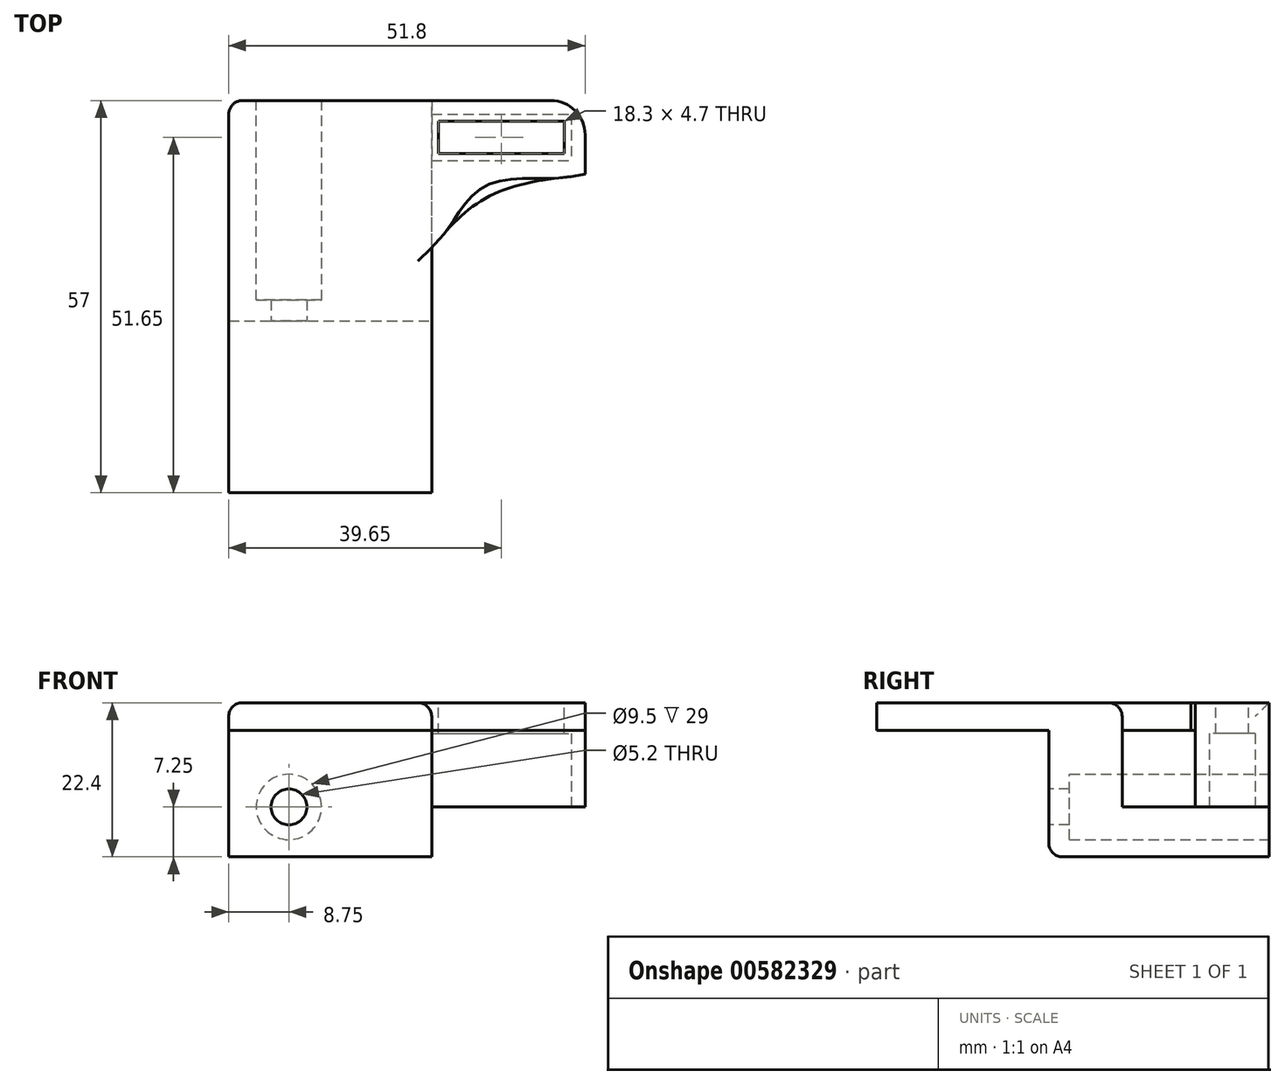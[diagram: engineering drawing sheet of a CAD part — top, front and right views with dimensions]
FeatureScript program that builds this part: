
annotation { "Feature Type Name" : "Feature", "Feature Type Description" : "" }
export const myFeature = defineFeature(function(context is Context, id is Id, definition is map)
    precondition{}
    {
        {
            var Q0;
            Q0=qCreatedBy(makeId("Front.planeOp"),FACE);
            var sketch = newSketch(context, id + "F0", { "sketchPlane" : qUnion([Q0])});
            skLineSegment(sketch, "E0.bottom", {"start": v(8.75, 10.25) * mm, "end": v(-8.75, 10.25) * mm});
            skLineSegment(sketch, "E0.top", {"start": v(8.75, -10.25) * mm, "end": v(3.25, -10.25) * mm});
            skLineSegment(sketch, "E0.left", {"start": v(8.75, 10.25) * mm, "end": v(8.75, -10.25) * mm});
            skLineSegment(sketch, "E0.right", {"start": v(-8.75, 10.25) * mm, "end": v(-8.75, 1.75) * mm});
            skPoint(sketch, "E0.middle", {"position": v(0, 0) * mm});
            skCircle(sketch, "E1", {"center": v(0, 0) * mm, "radius": 4.75 * mm});
            skLineSegment(sketch, "E2", {"start": v(8.75, 10.25) * mm, "end": v(20.75, 10.25) * mm});
            skLineSegment(sketch, "E3", {"start": v(20.75, 10.25) * mm, "end": v(20.75, -10.25) * mm});
            skLineSegment(sketch, "E4", {"start": v(8.75, -10.25) * mm, "end": v(20.75, -10.25) * mm});
            skPoint(sketch, "E5.visualSharp", {"position": v(-8.75, -10.25) * mm});
            skLineSegment(sketch, "E6", {"start": v(-8.75, 1.75) * mm, "end": v(-8.75, -10.25) * mm});
            skLineSegment(sketch, "E7", {"start": v(3.25, -10.25) * mm, "end": v(-8.75, -10.25) * mm});
            skSolve(sketch);
        }
        {
            var Q0;
            Q0 = qSketchRegion(id + "F0", true);
            extrude(context, id + "F1", {"entities" : qUnion([Q0]), "depth" : 30 * mm, "offsetDistance" : 25 * mm});
        }
        {
            var Q0;
            Q0=makeQuery(id+"F1.opExtrude","SWEPT_FACE",FACE,{"disambiguationData":[OSD([sQuery(id+"F0.wireOp",EDGE,"E0.top"),sQuery(id+"F0.wireOp",EDGE,"E4")])]});
            cPlane(context, id + "F2", {"entities" : qUnion([Q0]), "cplaneType" : CPlaneType.OFFSET, "offset" : 10.25 * mm, "oppositeDirection" : true, "width" : 150 * mm, "height" : 150 * mm});
        }
        {
            var Q0;
            Q0=qCreatedBy(id+"F2.planeOp",FACE);
            var sketch = newSketch(context, id + "F3", { "sketchPlane" : qUnion([Q0])});
            skLineSegment(sketch, "E8.bottom", {"start": v(20.75, 0) * mm, "end": v(41.05, 0) * mm});
            skLineSegment(sketch, "E8.top", {"start": v(20.75, 6.7) * mm, "end": v(41.05, 6.7) * mm});
            skLineSegment(sketch, "E8.left", {"start": v(20.75, 0) * mm, "end": v(20.75, 6.7) * mm});
            skLineSegment(sketch, "E8.right", {"start": v(41.05, 0) * mm, "end": v(41.05, 6.7) * mm});
            skLineSegment(sketch, "E9.0", {"start": v(18.75, -2) * mm, "end": v(43.05, -2) * mm});
            skLineSegment(sketch, "E9.1", {"start": v(18.75, -2) * mm, "end": v(18.75, 8.7) * mm});
            skLineSegment(sketch, "E9.2", {"start": v(18.75, 8.7) * mm, "end": v(43.05, 8.7) * mm});
            skLineSegment(sketch, "E9.3", {"start": v(43.05, -2) * mm, "end": v(43.05, 8.7) * mm});
            skSolve(sketch);
        }
        {
            var Q0;
            Q0 = qSketchRegion(id + "F3", true);
            extrude(context, id + "F4", {"entities" : qUnion([Q0]), "operationType" : NewBodyOperationType.ADD, "oppositeDirection" : true, "depth" : 11.15 * mm, "offsetDistance" : 25 * mm});
        }
        {
            var Q0;
            Q0=makeQuery(id+"F4.opExtrude","CAP_FACE",FACE,{"disambiguationData":[OSD([sQuery(id+"F3.wireOp",EDGE,"E8.bottom"),sQuery(id+"F3.wireOp",EDGE,"E8.top"),sQuery(id+"F3.wireOp",EDGE,"E8.left"),sQuery(id+"F3.wireOp",EDGE,"E8.right"),sQuery(id+"F3.wireOp",EDGE,"E9.0"),sQuery(id+"F3.wireOp",EDGE,"E9.1"),sQuery(id+"F3.wireOp",EDGE,"E9.2"),sQuery(id+"F3.wireOp",EDGE,"E9.3")])],"isStart":false});
            var sketch = newSketch(context, id + "F5", { "sketchPlane" : qUnion([Q0])});
            skLineSegment(sketch, "E10.0", {"start": v(40.05, -1) * mm, "end": v(40.05, -5.7) * mm});
            skLineSegment(sketch, "E10.1", {"start": v(21.75, -1) * mm, "end": v(40.05, -1) * mm});
            skLineSegment(sketch, "E10.2", {"start": v(21.75, -1) * mm, "end": v(21.75, -5.7) * mm});
            skLineSegment(sketch, "E11.0", {"start": v(21.75, -5.7) * mm, "end": v(40.05, -5.7) * mm});
            skSolve(sketch);
        }
        {
            var Q0;
            Q0=makeQuery(id+"F5.imprint","IMPRINT",FACE,{"disambiguationData":[TD([[makeQuery(id+"F5.imprint","IMPRINT",EDGE,{"derivedFrom":sQuery(id+"F5.wireOp",EDGE,"E10.0")}),1.0]])]});
            extrude(context, id + "F6", {"entities" : qUnion([Q0]), "operationType" : NewBodyOperationType.ADD, "oppositeDirection" : true, "depth" : 0.5 * mm, "offsetDistance" : 25 * mm});
        }
        {
            var Q0;
            Q0=makeQuery(id+"F1.opExtrude","CAP_FACE",FACE,{"disambiguationData":[OSD([sQuery(id+"F0.wireOp",EDGE,"E0.bottom"),sQuery(id+"F0.wireOp",EDGE,"E0.top"),sQuery(id+"F0.wireOp",EDGE,"E0.right"),sQuery(id+"F0.wireOp",EDGE,"E1"),sQuery(id+"F0.wireOp",EDGE,"E2"),sQuery(id+"F0.wireOp",EDGE,"E3"),sQuery(id+"F0.wireOp",EDGE,"E4"),sQuery(id+"F0.wireOp",EDGE,"E5.filletArc")])],"isStart":true});
            var sketch = newSketch(context, id + "F7", { "sketchPlane" : qUnion([Q0])});
            skLineSegment(sketch, "E12.0", {"start": v(8.75, 10.25) * mm, "end": v(-18.75, 10.25) * mm});
            skLineSegment(sketch, "E13.0", {"start": v(8.75, 10.25) * mm, "end": v(8.75, 10.25) * mm});
            skLineSegment(sketch, "E14.0", {"start": v(-3.25, -10.25) * mm, "end": v(-20.75, -10.25) * mm});
            skPoint(sketch, "E15.0", {"position": v(-20.75, -5.12) * mm});
            skLineSegment(sketch, "E16.0", {"start": v(-20.75, 0) * mm, "end": v(-20.75, -10.25) * mm});
            skLineSegment(sketch, "E17.0.0", {"start": v(-20.75, 0) * mm, "end": v(-18.75, 0) * mm});
            skLineSegment(sketch, "E17.0.1", {"start": v(-18.75, 0) * mm, "end": v(-18.75, 10.25) * mm});
            skCircle(sketch, "E18.0", {"center": v(0, 0) * mm, "radius": 4.75 * mm});
            skPoint(sketch, "E17.0.2.end.orphan", {"position": v(-43.05, 11.15) * mm});
            skPoint(sketch, "E17.0.2.start.orphan", {"position": v(-18.75, 11.15) * mm});
            skPoint(sketch, "E19.orphan", {"position": v(-43.05, 0) * mm});
            skLineSegment(sketch, "E20.0", {"start": v(8.75, 10.25) * mm, "end": v(8.75, -10.25) * mm});
            skLineSegment(sketch, "E21.0", {"start": v(8.75, -10.25) * mm, "end": v(-20.75, -10.25) * mm});
            skSolve(sketch);
        }
        {
            var Q0;
            Q0 = qSketchRegion(id + "F7", true);
            extrude(context, id + "F8", {"entities" : qUnion([Q0]), "operationType" : NewBodyOperationType.ADD, "depth" : 2 * mm, "offsetDistance" : 25 * mm});
        }
        {
            var Q0;
            Q0=makeQuery(id+"F8.boolean.opBoolean","MERGE",FACE,{"derivedFrom":[makeQuery(id+"F1.opExtrude","SWEPT_FACE",FACE,{"disambiguationData":[OSD([sQuery(id+"F0.wireOp",EDGE,"E0.bottom"),sQuery(id+"F0.wireOp",EDGE,"E2")])]}),makeQuery(id+"F8.opExtrude","SWEPT_FACE",FACE,{"disambiguationData":[OSD([sQuery(id+"F7.wireOp",EDGE,"E12.0")])]})]});
            var sketch = newSketch(context, id + "F9", { "sketchPlane" : qUnion([Q0])});
            skLineSegment(sketch, "E22.0", {"start": v(18.75, -8.7) * mm, "end": v(18.75, 2) * mm});
            skLineSegment(sketch, "E23.0", {"start": v(18.75, -8.7) * mm, "end": v(20.75, -8.7) * mm});
            skLineSegment(sketch, "E24.0", {"start": v(20.75, -30) * mm, "end": v(20.75, -8.7) * mm});
            skLineSegment(sketch, "E25.0", {"start": v(-8.75, 2) * mm, "end": v(18.75, 2) * mm});
            skLineSegment(sketch, "E26.0", {"start": v(-8.75, -30) * mm, "end": v(-8.75, 2) * mm});
            skLineSegment(sketch, "E27.0", {"start": v(-8.75, -30) * mm, "end": v(20.75, -30) * mm});
            skPoint(sketch, "E28.orphan", {"position": v(43.05, -8.7) * mm});
            skSolve(sketch);
        }
        {
            var Q0;
            Q0 = qSketchRegion(id + "F9", true);
            var Q1;
            {var subQ0=sQuery(id+"F3.wireOp",EDGE,"E8.right");var subQ1=sQuery(id+"F3.wireOp",EDGE,"E8.left");var subQ2=sQuery(id+"F3.wireOp",EDGE,"E8.top");var subQ3=sQuery(id+"F3.wireOp",EDGE,"E8.bottom");Q1=makeQuery(id+"F6.boolean.opBoolean","MERGE",FACE,{"derivedFrom":[makeQuery(id+"F4.opExtrude","CAP_FACE",FACE,{"disambiguationData":[OSD([subQ3,subQ2,subQ1,subQ0,sQuery(id+"F3.wireOp",EDGE,"E9.0"),sQuery(id+"F3.wireOp",EDGE,"E9.1"),sQuery(id+"F3.wireOp",EDGE,"E9.2"),sQuery(id+"F3.wireOp",EDGE,"E9.3")])],"isStart":false}),makeQuery(id+"F6.opExtrude","CAP_FACE",FACE,{"disambiguationData":[OSD([subQ3,subQ2,subQ1,subQ0,sQuery(id+"F5.wireOp",EDGE,"E10.0"),sQuery(id+"F5.wireOp",EDGE,"E10.1"),sQuery(id+"F5.wireOp",EDGE,"E10.2"),sQuery(id+"F5.wireOp",EDGE,"E11.0")])],"isStart":true})]});}
            extrude(context, id + "F10", {"entities" : qUnion([Q0]), "operationType" : NewBodyOperationType.ADD, "endBound" : BoundingType.UP_TO_SURFACE, "depth" : 1 * mm, "endBoundEntityFace" : qUnion([Q1]), "offsetDistance" : 25 * mm});
        }
        {
            var Q0;
            {var subQ0=sQuery(id+"F5.wireOp",EDGE,"E11.0");var subQ1=sQuery(id+"F5.wireOp",EDGE,"E10.2");var subQ2=sQuery(id+"F5.wireOp",EDGE,"E10.1");var subQ3=sQuery(id+"F5.wireOp",EDGE,"E10.0");var subQ4=sQuery(id+"F3.wireOp",EDGE,"E9.3");var subQ5=sQuery(id+"F3.wireOp",EDGE,"E9.2");var subQ6=sQuery(id+"F3.wireOp",EDGE,"E9.1");var subQ7=sQuery(id+"F3.wireOp",EDGE,"E9.0");var subQ8=sQuery(id+"F3.wireOp",EDGE,"E8.right");var subQ9=sQuery(id+"F3.wireOp",EDGE,"E8.left");var subQ10=sQuery(id+"F3.wireOp",EDGE,"E8.top");var subQ11=sQuery(id+"F3.wireOp",EDGE,"E8.bottom");Q0=makeQuery(id+"F10.boolean.opBoolean","MERGE",FACE,{"derivedFrom":[makeQuery(id+"F6.boolean.opBoolean","MERGE",FACE,{"derivedFrom":[makeQuery(id+"F4.opExtrude","CAP_FACE",FACE,{"disambiguationData":[OSD([subQ11,subQ10,subQ9,subQ8,subQ7,subQ6,subQ5,subQ4])],"isStart":false}),makeQuery(id+"F6.opExtrude","CAP_FACE",FACE,{"disambiguationData":[OSD([subQ11,subQ10,subQ9,subQ8,subQ3,subQ2,subQ1,subQ0])],"isStart":true})]}),makeQuery(id+"F10.opExtrude","CAP_FACE",FACE,{"disambiguationData":[OSD([subQ11,subQ10,subQ9,subQ8,subQ7,subQ6,subQ5,subQ4,subQ3,subQ2,subQ1,subQ0])],"isStart":false})]});}
            var sketch = newSketch(context, id + "F11", { "sketchPlane" : qUnion([Q0])});
            skPoint(sketch, "E29.endSnap0", {"position": v(20.75, -19.35) * mm});
            skFitSpline(sketch, "E30", {"points": [v(43.05, -8.7) * mm, v(29.05, -11.93) * mm, v(20.75, -19.35) * mm], "startDerivative": vector(-28.6, -3.49) * mm, "endDerivative": vector(-15.73, -18.12) * mm});
            skLineSegment(sketch, "E31", {"start": v(20.75, -19.35) * mm, "end": v(20.75, -8.7) * mm});
            skLineSegment(sketch, "E32", {"start": v(20.75, -8.7) * mm, "end": v(43.05, -8.7) * mm});
            skSolve(sketch);
        }
        {
            var Q0;
            Q0 = qSketchRegion(id + "F11", true);
            var Q1;
            Q1=qCreatedBy(makeId("Top.planeOp"),FACE);
            extrude(context, id + "F12", {"entities" : qUnion([Q0]), "operationType" : NewBodyOperationType.ADD, "endBound" : BoundingType.UP_TO_SURFACE, "oppositeDirection" : true, "depth" : 25 * mm, "endBoundEntityFace" : qUnion([Q1]), "offsetDistance" : 25 * mm});
        }
        {
            var Q0;
            Q0=makeQuery(id+"F10.boolean.opBoolean","MERGE",FACE,{"derivedFrom":[makeQuery(id+"F1.opExtrude","CAP_FACE",FACE,{"disambiguationData":[OSD([sQuery(id+"F0.wireOp",EDGE,"E0.bottom"),sQuery(id+"F0.wireOp",EDGE,"E0.top"),sQuery(id+"F0.wireOp",EDGE,"E0.right"),sQuery(id+"F0.wireOp",EDGE,"E1"),sQuery(id+"F0.wireOp",EDGE,"E2"),sQuery(id+"F0.wireOp",EDGE,"E3"),sQuery(id+"F0.wireOp",EDGE,"E4"),sQuery(id+"F0.wireOp",EDGE,"E5.filletArc")])],"isStart":false}),makeQuery(id+"F10.opExtrude","SWEPT_FACE",FACE,{"disambiguationData":[OSD([sQuery(id+"F9.wireOp",EDGE,"E27.0")])]})]});
            var sketch = newSketch(context, id + "F13", { "sketchPlane" : qUnion([Q0])});
            skCircle(sketch, "E33", {"center": v(0, 0) * mm, "radius": 2.6 * mm});
            skCircle(sketch, "E34.0", {"center": v(0, 0) * mm, "radius": 4.75 * mm});
            skSolve(sketch);
        }
        {
            var Q0;
            Q0 = qSketchRegion(id + "F13", true);
            extrude(context, id + "F14", {"entities" : qUnion([Q0]), "operationType" : NewBodyOperationType.ADD, "oppositeDirection" : true, "depth" : 3 * mm, "offsetDistance" : 25 * mm});
        }
        {
            var Q0;
            Q0=makeQuery(id+"F14.boolean.opBoolean","MERGE",FACE,{"derivedFrom":[makeQuery(id+"F10.boolean.opBoolean","MERGE",FACE,{"derivedFrom":[makeQuery(id+"F1.opExtrude","CAP_FACE",FACE,{"disambiguationData":[OSD([sQuery(id+"F0.wireOp",EDGE,"E0.bottom"),sQuery(id+"F0.wireOp",EDGE,"E0.top"),sQuery(id+"F0.wireOp",EDGE,"E0.right"),sQuery(id+"F0.wireOp",EDGE,"E1"),sQuery(id+"F0.wireOp",EDGE,"E2"),sQuery(id+"F0.wireOp",EDGE,"E3"),sQuery(id+"F0.wireOp",EDGE,"E4"),sQuery(id+"F0.wireOp",EDGE,"E5.filletArc")])],"isStart":false}),makeQuery(id+"F10.opExtrude","SWEPT_FACE",FACE,{"disambiguationData":[OSD([sQuery(id+"F9.wireOp",EDGE,"E27.0")])]})]}),makeQuery(id+"F14.opExtrude","CAP_FACE",FACE,{"disambiguationData":[OSD([sQuery(id+"F13.wireOp",EDGE,"E33"),sQuery(id+"F13.wireOp",EDGE,"E34.0")])],"isStart":true})]});
            var sketch = newSketch(context, id + "F15", { "sketchPlane" : qUnion([Q0])});
            skLineSegment(sketch, "E35.bottom", {"start": v(-8.75, 11.15) * mm, "end": v(20.75, 11.15) * mm});
            skLineSegment(sketch, "E35.top", {"start": v(-8.75, 15.15) * mm, "end": v(20.75, 15.15) * mm});
            skLineSegment(sketch, "E35.left", {"start": v(-8.75, 11.15) * mm, "end": v(-8.75, 15.15) * mm});
            skLineSegment(sketch, "E35.right", {"start": v(20.75, 11.15) * mm, "end": v(20.75, 15.15) * mm});
            skSolve(sketch);
        }
        {
            var Q0;
            Q0 = qSketchRegion(id + "F15", true);
            extrude(context, id + "F16", {"entities" : qUnion([Q0]), "operationType" : NewBodyOperationType.ADD, "depth" : 25 * mm, "offsetDistance" : 25 * mm, "hasSecondDirection" : true, "secondDirectionOppositeDirection" : true, "secondDirectionDepth" : 10 * mm});
        }
        {
            var Q0;
            {var subQ0=sQuery(id+"F5.wireOp",EDGE,"E11.0");var subQ1=sQuery(id+"F5.wireOp",EDGE,"E10.2");var subQ2=sQuery(id+"F5.wireOp",EDGE,"E10.1");var subQ3=sQuery(id+"F5.wireOp",EDGE,"E10.0");var subQ4=sQuery(id+"F3.wireOp",EDGE,"E9.3");var subQ5=sQuery(id+"F3.wireOp",EDGE,"E9.2");var subQ6=sQuery(id+"F3.wireOp",EDGE,"E9.1");var subQ7=sQuery(id+"F3.wireOp",EDGE,"E9.0");var subQ8=sQuery(id+"F3.wireOp",EDGE,"E8.right");var subQ9=sQuery(id+"F3.wireOp",EDGE,"E8.left");var subQ10=sQuery(id+"F3.wireOp",EDGE,"E8.top");var subQ11=sQuery(id+"F3.wireOp",EDGE,"E8.bottom");Q0=makeQuery(id+"F12.boolean.opBoolean","MERGE",FACE,{"derivedFrom":[makeQuery(id+"F10.boolean.opBoolean","MERGE",FACE,{"derivedFrom":[makeQuery(id+"F6.boolean.opBoolean","MERGE",FACE,{"derivedFrom":[makeQuery(id+"F4.opExtrude","CAP_FACE",FACE,{"disambiguationData":[OSD([subQ11,subQ10,subQ9,subQ8,subQ7,subQ6,subQ5,subQ4])],"isStart":false}),makeQuery(id+"F6.opExtrude","CAP_FACE",FACE,{"disambiguationData":[OSD([subQ11,subQ10,subQ9,subQ8,subQ3,subQ2,subQ1,subQ0])],"isStart":true})]}),makeQuery(id+"F10.opExtrude","CAP_FACE",FACE,{"disambiguationData":[OSD([subQ11,subQ10,subQ9,subQ8,subQ7,subQ6,subQ5,subQ4,subQ3,subQ2,subQ1,subQ0])],"isStart":false})]}),makeQuery(id+"F12.opExtrude","CAP_FACE",FACE,{"disambiguationData":[OSD([sQuery(id+"F11.wireOp",EDGE,"E30"),sQuery(id+"F11.wireOp",EDGE,"E31"),sQuery(id+"F11.wireOp",EDGE,"E32")])],"isStart":true})]});}
            var sketch = newSketch(context, id + "F17", { "sketchPlane" : qUnion([Q0])});
            skLineSegment(sketch, "E36.0", {"start": v(-8.75, -20) * mm, "end": v(20.75, -20) * mm});
            skPoint(sketch, "E37.0", {"position": v(20.75, -19.67) * mm});
            skSolve(sketch);
        }
        {
            var Q0;
            Q0=makeQuery(id+"F17.imprint","IMPRINT",FACE,{"disambiguationData":[TD([[makeQuery(id+"F17.imprint","IMPRINT",EDGE,{"derivedFrom":sQuery(id+"F17.wireOp",EDGE,"E36.0")}),-1.0]])]});
            var sketch = newSketch(context, id + "F18", { "sketchPlane" : qUnion([Q0])});
            skLineSegment(sketch, "E38.0", {"start": v(-8.75, -20) * mm, "end": v(20.75, -20) * mm});
            skLineSegment(sketch, "E39.0", {"start": v(20.75, -19.35) * mm, "end": v(20.75, -20) * mm});
            skFitSpline(sketch, "E40.0", {"points": [v(43.05, -8.7) * mm, v(37.98, -9.32) * mm, v(28.45, -10.48) * mm, v(23.2, -16.52) * mm, v(20.75, -19.35) * mm]});
            skLineSegment(sketch, "E41.0", {"start": v(-3.75, 2) * mm, "end": v(38.05, 2) * mm});
            skLineSegment(sketch, "E42.0", {"start": v(-8.75, -3) * mm, "end": v(-8.75, -20) * mm});
            skLineSegment(sketch, "E43.0", {"start": v(21.75, -5.7) * mm, "end": v(40.05, -5.7) * mm});
            skLineSegment(sketch, "E44.0", {"start": v(40.05, -1) * mm, "end": v(40.05, -5.7) * mm});
            skLineSegment(sketch, "E45.0", {"start": v(21.75, -1) * mm, "end": v(40.05, -1) * mm});
            skPoint(sketch, "E46.0", {"position": v(21.75, -3.35) * mm});
            skLineSegment(sketch, "E47.0", {"start": v(21.75, -1) * mm, "end": v(21.75, -5.7) * mm});
            skFitSpline(sketch, "E48.0", {"points": [v(43.05, -8.7) * mm, v(37.98, -9.32) * mm, v(28.45, -10.48) * mm, v(23.2, -16.52) * mm, v(20.75, -19.35) * mm]});
            skLineSegment(sketch, "E49.0", {"start": v(43.05, 2) * mm, "end": v(43.05, -8.7) * mm});
            skLineSegment(sketch, "E50.0", {"start": v(-8.75, 2) * mm, "end": v(43.05, 2) * mm});
            skLineSegment(sketch, "E51.0", {"start": v(-8.75, 2) * mm, "end": v(-8.75, -20) * mm});
            skSolve(sketch);
        }
        {
            var Q0;
            Q0 = qSketchRegion(id + "F18", true);
            var Q1;
            Q1=makeQuery(id+"F16.opExtrude","SWEPT_FACE",FACE,{"disambiguationData":[OSD([sQuery(id+"F15.wireOp",EDGE,"E35.top")])]});
            extrude(context, id + "F19", {"entities" : qUnion([Q0]), "operationType" : NewBodyOperationType.ADD, "endBound" : BoundingType.UP_TO_SURFACE, "depth" : 25 * mm, "endBoundEntityFace" : qUnion([Q1]), "offsetDistance" : 25 * mm});
        }
        {
            var Q0;
            Q0=makeQuery(id+"F19.boolean.opBoolean","MERGE",FACE,{"derivedFrom":[makeQuery(id+"F10.boolean.opBoolean","MERGE",FACE,{"derivedFrom":[makeQuery(id+"F8.boolean.opBoolean","MERGE",FACE,{"derivedFrom":[makeQuery(id+"F4.opExtrude","SWEPT_FACE",FACE,{"disambiguationData":[OSD([sQuery(id+"F3.wireOp",EDGE,"E9.0")])]}),makeQuery(id+"F8.opExtrude","CAP_FACE",FACE,{"disambiguationData":[OSD([sQuery(id+"F7.wireOp",EDGE,"E12.0"),sQuery(id+"F7.wireOp",EDGE,"E13.0"),sQuery(id+"F7.wireOp",EDGE,"35ee3434-dcd9-4027-9f40-7a7ec9be7b3f.0"),sQuery(id+"F7.wireOp",EDGE,"E14.0"),sQuery(id+"F7.wireOp",EDGE,"E16.0"),sQuery(id+"F7.wireOp",EDGE,"E17.0.0"),sQuery(id+"F7.wireOp",EDGE,"E17.0.1"),sQuery(id+"F7.wireOp",EDGE,"E18.0")])],"isStart":false})]}),makeQuery(id+"F10.opExtrude","SWEPT_FACE",FACE,{"disambiguationData":[OSD([sQuery(id+"F9.wireOp",EDGE,"E25.0")])]})]}),makeQuery(id+"F19.opExtrude","SWEPT_FACE",FACE,{"disambiguationData":[OSD([sQuery(id+"F18.wireOp",EDGE,"E41.0")])]})]});
            var sketch = newSketch(context, id + "F20", { "sketchPlane" : qUnion([Q0])});
            skSolve(sketch);
        }
        {
            var Q0;
            Q0=makeQuery(id+"F20.imprint","IMPRINT",FACE,{"disambiguationData":[TD([[makeQuery(id+"F20.imprint","IMPRINT",EDGE,{"derivedFrom":makeQuery(id+"F8.opExtrude","CAP_EDGE",EDGE,{"disambiguationData":[OSD([sQuery(id+"F7.wireOp",EDGE,"E16.0")])],"isStart":false})}),1.0]])]});
            var sketch = newSketch(context, id + "F21", { "sketchPlane" : qUnion([Q0])});
            skLineSegment(sketch, "E52.0", {"start": v(8.75, -10.25) * mm, "end": v(-20.75, -10.25) * mm});
            skLineSegment(sketch, "E53.0", {"start": v(-20.75, -7.25) * mm, "end": v(-20.75, -10.25) * mm});
            skLineSegment(sketch, "E54.0", {"start": v(8.75, -7.25) * mm, "end": v(8.75, -10.25) * mm});
            skLineSegment(sketch, "E55", {"start": v(-20.75, -7.25) * mm, "end": v(8.75, -7.25) * mm});
            skPoint(sketch, "E56.orphan", {"position": v(-20.75, 0) * mm});
            skPoint(sketch, "E57.orphan", {"position": v(8.75, 15.15) * mm});
            skSolve(sketch);
        }
        {
            var Q0;
            Q0 = qSketchRegion(id + "F21", true);
            extrude(context, id + "F22", {"entities" : qUnion([Q0]), "operationType" : NewBodyOperationType.REMOVE, "endBound" : BoundingType.THROUGH_ALL, "oppositeDirection" : true, "depth" : 25 * mm, "offsetDistance" : 25 * mm});
        }
        {
            var Q0;
            Q0=makeQuery(id+"F19.boolean.opBoolean","MERGE",EDGE,{"derivedFrom":[makeQuery(id+"F4.opExtrude","SWEPT_EDGE",EDGE,{"disambiguationData":[OSD([sQuery(id+"F3.wireOp",EDGE,"E9.0"),sQuery(id+"F3.wireOp",EDGE,"E9.3")])]}),makeQuery(id+"F19.opExtrude","SWEPT_EDGE",EDGE,{"disambiguationData":[OSD([sQuery(id+"F18.wireOp",EDGE,"E49.0"),sQuery(id+"F18.wireOp",EDGE,"E50.0")])]})]});
            var Q1;
            {var subQ0=sQuery(id+"F3.wireOp",EDGE,"E9.3");Q1=makeQuery(id+"F19.boolean.opBoolean","MERGE",EDGE,{"derivedFrom":[makeQuery(id+"F12.boolean.opBoolean","MERGE",EDGE,{"derivedFrom":[makeQuery(id+"F4.opExtrude","SWEPT_EDGE",EDGE,{"disambiguationData":[OSD([sQuery(id+"F3.wireOp",EDGE,"E9.2"),subQ0])]}),makeQuery(id+"F12.opExtrude","SWEPT_EDGE",EDGE,{"disambiguationData":[OSD([subQ0,sQuery(id+"F11.wireOp",EDGE,"E30"),sQuery(id+"F11.wireOp",EDGE,"E32")])]})]}),makeQuery(id+"F19.opExtrude","SWEPT_EDGE",EDGE,{"disambiguationData":[OSD([sQuery(id+"F18.wireOp",EDGE,"E48.0"),sQuery(id+"F18.wireOp",EDGE,"E49.0")])]})]});}
            fillet(context, id + "F23", {"entities" : qUnion([Q0, Q1]), "radius" : 5 * mm, "tangentPropagation" : true, "allowEdgeOverflow" : false});
        }
        {
            var Q0;
            Q0=makeQuery(id+"F22.boolean.opBoolean","COPY",EDGE,{"derivedFrom":makeQuery(id+"F22.opExtrude","CAP_EDGE",EDGE,{"disambiguationData":[OSD([sQuery(id+"F21.wireOp",EDGE,"E55")])],"isStart":true})});
            var Q1;
            Q1=makeQuery(id+"F19.boolean.opBoolean","MERGE",EDGE,{"derivedFrom":[makeQuery(id+"F10.boolean.opBoolean","MERGE",EDGE,{"derivedFrom":[makeQuery(id+"F8.opExtrude","CAP_EDGE",EDGE,{"disambiguationData":[OSD([sQuery(id+"F7.wireOp",EDGE,"E20.0")])],"isStart":false}),makeQuery(id+"F10.opExtrude","SWEPT_EDGE",EDGE,{"disambiguationData":[OSD([sQuery(id+"F9.wireOp",EDGE,"E25.0"),sQuery(id+"F9.wireOp",EDGE,"E26.0")])]})]}),makeQuery(id+"F19.opExtrude","SWEPT_EDGE",EDGE,{"disambiguationData":[OSD([sQuery(id+"F18.wireOp",EDGE,"E50.0"),sQuery(id+"F18.wireOp",EDGE,"E51.0")])]})]});
            var Q2;
            Q2=makeQuery(id+"F22.boolean.opBoolean","COPY",EDGE,{"derivedFrom":makeQuery(id+"F22.opExtrude","SWEPT_EDGE",EDGE,{"disambiguationData":[OSD([sQuery(id+"F7.wireOp",EDGE,"E20.0"),sQuery(id+"F9.wireOp",EDGE,"E25.0"),sQuery(id+"F9.wireOp",EDGE,"E26.0"),sQuery(id+"F18.wireOp",EDGE,"E50.0"),sQuery(id+"F18.wireOp",EDGE,"E51.0"),sQuery(id+"F21.wireOp",EDGE,"E54.0"),sQuery(id+"F21.wireOp",EDGE,"E55")])]})});
            var Q3;
            Q3=makeQuery(id+"F22.boolean.opBoolean","INTERSECT",EDGE,{"derivedFrom":[makeQuery(id+"F14.boolean.opBoolean","MERGE",FACE,{"derivedFrom":[makeQuery(id+"F10.boolean.opBoolean","MERGE",FACE,{"derivedFrom":[makeQuery(id+"F1.opExtrude","CAP_FACE",FACE,{"disambiguationData":[OSD([sQuery(id+"F0.wireOp",EDGE,"E0.bottom"),sQuery(id+"F0.wireOp",EDGE,"E0.top"),sQuery(id+"F0.wireOp",EDGE,"E0.right"),sQuery(id+"F0.wireOp",EDGE,"E1"),sQuery(id+"F0.wireOp",EDGE,"E2"),sQuery(id+"F0.wireOp",EDGE,"E3"),sQuery(id+"F0.wireOp",EDGE,"E4"),sQuery(id+"F0.wireOp",EDGE,"E6"),sQuery(id+"F0.wireOp",EDGE,"E7")])],"isStart":false}),makeQuery(id+"F10.opExtrude","SWEPT_FACE",FACE,{"disambiguationData":[OSD([sQuery(id+"F9.wireOp",EDGE,"E27.0")])]})]}),makeQuery(id+"F14.opExtrude","CAP_FACE",FACE,{"disambiguationData":[OSD([sQuery(id+"F13.wireOp",EDGE,"E33"),sQuery(id+"F13.wireOp",EDGE,"E34.0")])],"isStart":true})]}),makeQuery(id+"F22.opExtrude","SWEPT_FACE",FACE,{"disambiguationData":[OSD([sQuery(id+"F21.wireOp",EDGE,"E55")])]})]});
            var Q4;
            Q4=makeQuery(id+"F22.boolean.opBoolean","COPY",EDGE,{"derivedFrom":makeQuery(id+"F22.opExtrude","SWEPT_EDGE",EDGE,{"disambiguationData":[OSD([sQuery(id+"F7.wireOp",EDGE,"E16.0"),sQuery(id+"F21.wireOp",EDGE,"E53.0"),sQuery(id+"F21.wireOp",EDGE,"E55")])]})});
            var Q5;
            {var subQ0=sQuery(id+"F18.wireOp",EDGE,"E50.0");Q5=makeQuery(id+"F19.opExtrude","TWEAK_EDGE",EDGE,{"derivedFrom":[makeQuery(id+"F16.opExtrude","SWEPT_FACE",FACE,{"disambiguationData":[OSD([sQuery(id+"F15.wireOp",EDGE,"E35.top")])]}),makeQuery(id+"F18.imprint","IMPRINT",EDGE,{"disambiguationData":[TD([[makeQuery(id+"F18.imprint","INTERSECT",VERTEX,{"derivedFrom":[sQuery(id+"F18.wireOp",EDGE,"E49.0"),subQ0]}),1.0]])],"derivedFrom":subQ0})]});}
            var Q6;
            {var subQ0=sQuery(id+"F18.wireOp",EDGE,"E51.0");var subQ1=sQuery(id+"F15.wireOp",EDGE,"E35.top");Q6=makeQuery(id+"F19.boolean.opBoolean","MERGE",EDGE,{"derivedFrom":[makeQuery(id+"F16.opExtrude","SWEPT_EDGE",EDGE,{"disambiguationData":[OSD([subQ1,sQuery(id+"F15.wireOp",EDGE,"E35.left")])]}),makeQuery(id+"F19.opExtrude","TWEAK_EDGE",EDGE,{"derivedFrom":[makeQuery(id+"F16.opExtrude","SWEPT_FACE",FACE,{"disambiguationData":[OSD([subQ1])]}),makeQuery(id+"F18.imprint","IMPRINT",EDGE,{"disambiguationData":[TD([[makeQuery(id+"F18.imprint","INTERSECT",VERTEX,{"derivedFrom":[sQuery(id+"F18.wireOp",EDGE,"E50.0"),subQ0]}),-1.0]])],"derivedFrom":subQ0})]})]});}
            var Q7;
            {var subQ0=sQuery(id+"F15.wireOp",EDGE,"E35.top");Q7=makeQuery(id+"F19.boolean.opBoolean","MERGE",EDGE,{"derivedFrom":[makeQuery(id+"F16.opExtrude","SWEPT_EDGE",EDGE,{"disambiguationData":[OSD([subQ0,sQuery(id+"F15.wireOp",EDGE,"E35.right")])]}),makeQuery(id+"F19.opExtrude","TWEAK_EDGE",EDGE,{"derivedFrom":[makeQuery(id+"F16.opExtrude","SWEPT_FACE",FACE,{"disambiguationData":[OSD([subQ0])]}),makeQuery(id+"F18.imprint","IMPRINT",EDGE,{"derivedFrom":sQuery(id+"F18.wireOp",EDGE,"E39.0")})]})]});}
            fillet(context, id + "F24", {"entities" : qUnion([Q0, Q1, Q2, Q3, Q4, Q5, Q6, Q7]), "radius" : 2 * mm, "tangentPropagation" : true, "allowEdgeOverflow" : false});
        }
    });
